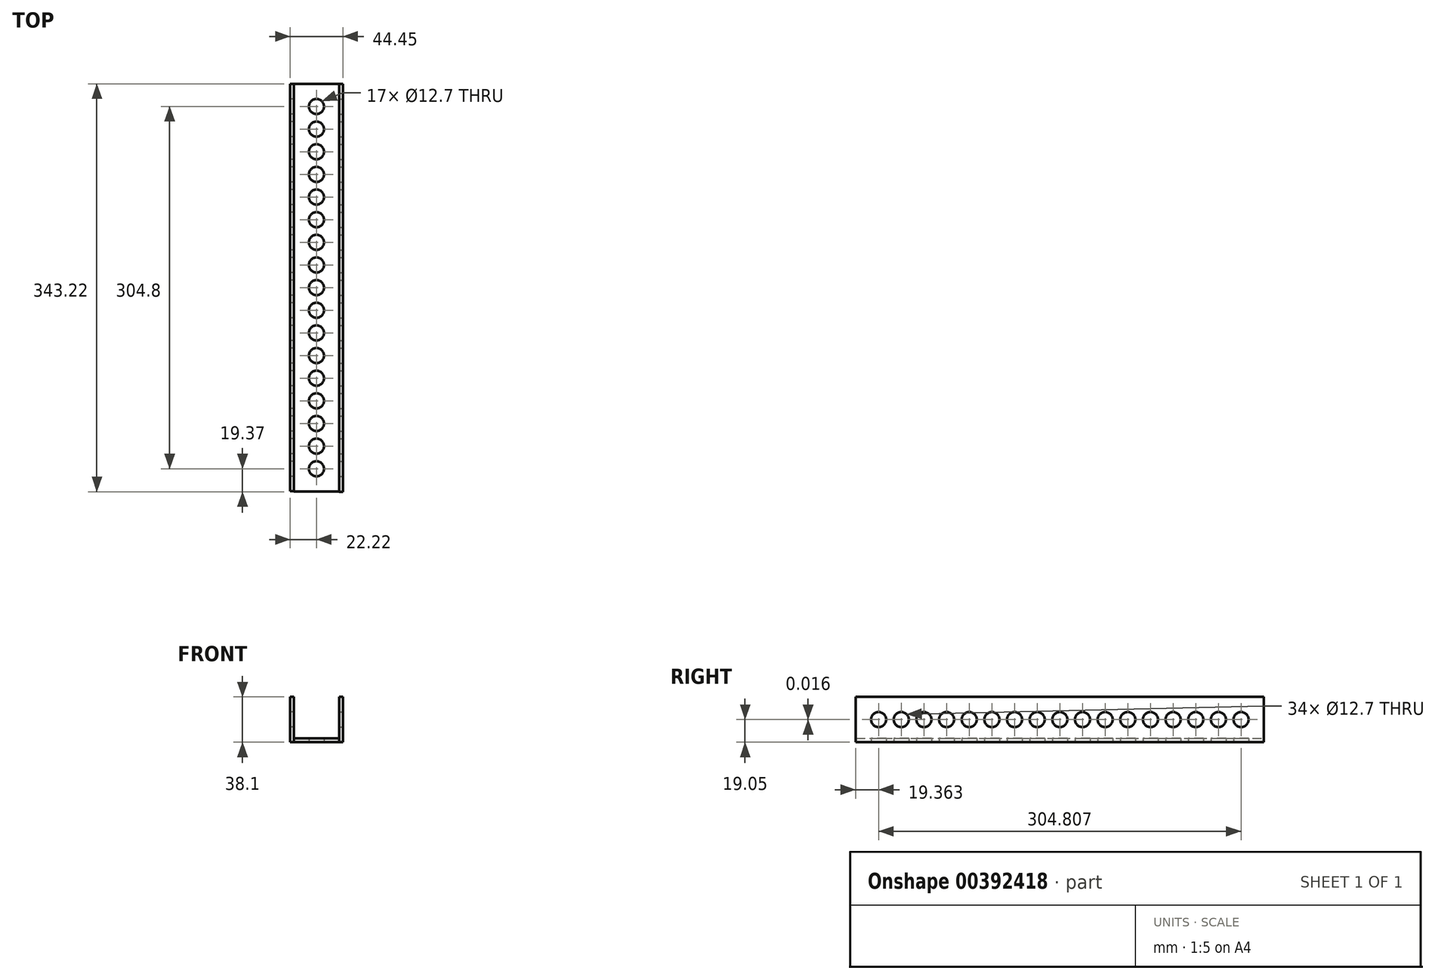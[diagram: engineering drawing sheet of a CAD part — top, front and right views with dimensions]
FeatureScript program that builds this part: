
annotation { "Feature Type Name" : "Feature", "Feature Type Description" : "" }
export const myFeature = defineFeature(function(context is Context, id is Id, definition is map)
    precondition{}
    {
        {
            var Q0;
            Q0=qCreatedBy(makeId("Top.planeOp"),FACE);
            var sketch = newSketch(context, id + "F0", { "sketchPlane" : qUnion([Q0])});
            skLineSegment(sketch, "E0.bottom", {"start": v(-89.28, 285.75) * mm, "end": v(-51.18, 285.75) * mm});
            skLineSegment(sketch, "E0.top", {"start": v(-89.28, -57.15) * mm, "end": v(-51.18, -57.15) * mm});
            skLineSegment(sketch, "E0.left", {"start": v(-89.28, 285.75) * mm, "end": v(-89.28, -57.15) * mm});
            skLineSegment(sketch, "E0.right", {"start": v(-51.18, 285.75) * mm, "end": v(-51.18, -57.15) * mm});
            skCircle(sketch, "E1", {"center": v(-70.23, 266.7) * mm, "radius": 6.35 * mm});
            skCircle(sketch, "E2", {"center": v(-70.23, 247.65) * mm, "radius": 6.35 * mm});
            skCircle(sketch, "E3", {"center": v(-70.23, 228.6) * mm, "radius": 6.35 * mm});
            skCircle(sketch, "E4", {"center": v(-70.23, 209.55) * mm, "radius": 6.35 * mm});
            skCircle(sketch, "E5", {"center": v(-70.23, 152.4) * mm, "radius": 6.35 * mm});
            skCircle(sketch, "E6", {"center": v(-70.23, 171.45) * mm, "radius": 6.35 * mm});
            skCircle(sketch, "E7", {"center": v(-70.23, 190.5) * mm, "radius": 6.35 * mm});
            skPoint(sketch, "E8", {"position": v(-89.28, 114.3) * mm});
            skCircle(sketch, "E9", {"center": v(-70.23, 95.25) * mm, "radius": 6.35 * mm});
            skCircle(sketch, "E10", {"center": v(-70.23, 76.2) * mm, "radius": 6.35 * mm});
            skCircle(sketch, "E11", {"center": v(-70.23, 114.3) * mm, "radius": 6.35 * mm});
            skCircle(sketch, "E12", {"center": v(-70.23, 57.15) * mm, "radius": 6.35 * mm});
            skCircle(sketch, "E13", {"center": v(-70.23, 0) * mm, "radius": 6.35 * mm});
            skCircle(sketch, "E14", {"center": v(-70.23, 38.1) * mm, "radius": 6.35 * mm});
            skCircle(sketch, "E15", {"center": v(-70.23, 19.05) * mm, "radius": 6.35 * mm});
            skCircle(sketch, "E16", {"center": v(-70.23, -38.1) * mm, "radius": 6.35 * mm});
            skCircle(sketch, "E17", {"center": v(-70.23, -19.05) * mm, "radius": 6.35 * mm});
            skPoint(sketch, "E18", {"position": v(-70.23, 285.75) * mm});
            skPoint(sketch, "E19", {"position": v(-70.23, -57.15) * mm});
            skLineSegment(sketch, "E20", {"start": v(-70.23, 285.75) * mm, "end": v(-70.23, -57.15) * mm});
            skLineSegment(sketch, "E21", {"start": v(-70.23, 266.7) * mm, "end": v(-70.23, 247.65) * mm});
            skLineSegment(sketch, "E22", {"start": v(-70.23, 247.65) * mm, "end": v(-70.23, 228.6) * mm});
            skLineSegment(sketch, "E23.bottom", {"start": v(-89.28, 285.75) * mm, "end": v(-92.45, 285.75) * mm});
            skLineSegment(sketch, "E23.top", {"start": v(-89.28, -57) * mm, "end": v(-92.45, -57) * mm});
            skLineSegment(sketch, "E23.left", {"start": v(-89.28, 285.75) * mm, "end": v(-89.28, -57) * mm});
            skLineSegment(sketch, "E23.right", {"start": v(-92.45, 285.75) * mm, "end": v(-92.45, -57) * mm});
            skCircle(sketch, "E24", {"center": v(-70.23, 133.35) * mm, "radius": 6.35 * mm});
            skLineSegment(sketch, "E25.bottom", {"start": v(-51.18, 285.75) * mm, "end": v(-48, 285.75) * mm});
            skLineSegment(sketch, "E25.top", {"start": v(-51.18, -57.47) * mm, "end": v(-48, -57.47) * mm});
            skLineSegment(sketch, "E25.left", {"start": v(-51.18, 285.75) * mm, "end": v(-51.18, -57.47) * mm});
            skLineSegment(sketch, "E25.right", {"start": v(-48, 285.75) * mm, "end": v(-48, -57.47) * mm});
            skSolve(sketch);
        }
        {
            var Q0;
            Q0 = qSketchRegion(id + "F0", true);
            extrude(context, id + "F1", {"entities" : qUnion([Q0]), "depth" : 3.17 * mm});
        }
        {
            var Q0;
            Q0=makeQuery(id+"F0.imprint","IMPRINT",FACE,{"disambiguationData":[TD([[makeQuery(id+"F0.imprint","IMPRINT",EDGE,{"derivedFrom":sQuery(id+"F0.wireOp",EDGE,"E23.bottom")}),1.0]])]});
            extrude(context, id + "F2", {"entities" : qUnion([Q0]), "operationType" : NewBodyOperationType.ADD, "depth" : 38.1 * mm});
        }
        {
            var Q0;
            {var subQ0=sQuery(id+"F0.wireOp",EDGE,"E23.right");Q0=makeQuery(id+"F2.boolean.opBoolean","MERGE",FACE,{"derivedFrom":[makeQuery(id+"F1.opExtrude","SWEPT_FACE",FACE,{"disambiguationData":[OSD([subQ0])]}),makeQuery(id+"F2.opExtrude","SWEPT_FACE",FACE,{"disambiguationData":[OSD([subQ0])]})]});}
            var sketch = newSketch(context, id + "F3", { "sketchPlane" : qUnion([Q0])});
            skCircle(sketch, "E26", {"center": v(-266.7, 19.05) * mm, "radius": 6.35 * mm});
            skPoint(sketch, "E27", {"position": v(-285.75, 19.05) * mm});
            skPoint(sketch, "E28", {"position": v(57, 19.05) * mm});
            skLineSegment(sketch, "E29", {"start": v(-285.75, 19.05) * mm, "end": v(57, 19.05) * mm});
            skCircle(sketch, "E30", {"center": v(-247.65, 19.05) * mm, "radius": 6.35 * mm});
            skCircle(sketch, "E31", {"center": v(-228.6, 19.05) * mm, "radius": 6.35 * mm});
            skCircle(sketch, "E32", {"center": v(-209.55, 19.05) * mm, "radius": 6.35 * mm});
            skCircle(sketch, "E33", {"center": v(-190.5, 19.05) * mm, "radius": 6.35 * mm});
            skCircle(sketch, "E34", {"center": v(-171.45, 19.05) * mm, "radius": 6.35 * mm});
            skCircle(sketch, "E35", {"center": v(-152.4, 19.05) * mm, "radius": 6.35 * mm});
            skCircle(sketch, "E36", {"center": v(0, 19.05) * mm, "radius": 6.35 * mm});
            skCircle(sketch, "E37", {"center": v(-19.05, 19.05) * mm, "radius": 6.35 * mm});
            skCircle(sketch, "E38", {"center": v(19.05, 19.07) * mm, "radius": 6.35 * mm});
            skCircle(sketch, "E39", {"center": v(-38.1, 19.05) * mm, "radius": 6.35 * mm});
            skCircle(sketch, "E40", {"center": v(-133.35, 19.05) * mm, "radius": 6.35 * mm});
            skCircle(sketch, "E41", {"center": v(-95.25, 19.05) * mm, "radius": 6.35 * mm});
            skCircle(sketch, "E42", {"center": v(38.1, 19.05) * mm, "radius": 6.35 * mm});
            skCircle(sketch, "E43", {"center": v(-76.2, 19.05) * mm, "radius": 6.35 * mm});
            skCircle(sketch, "E44", {"center": v(-114.3, 19.05) * mm, "radius": 6.35 * mm});
            skCircle(sketch, "E45", {"center": v(-57.15, 19.05) * mm, "radius": 6.35 * mm});
            skSolve(sketch);
        }
        {
            var Q0;
            Q0 = qSketchRegion(id + "F3", true);
            extrude(context, id + "F4", {"entities" : qUnion([Q0]), "operationType" : NewBodyOperationType.REMOVE, "oppositeDirection" : true, "depth" : 12.7 * mm});
        }
        {
            var Q0;
            {var subQ3=sQuery(id+"F0.wireOp",EDGE,"E25.bottom");Q0=makeQuery(id+"F0.imprint","IMPRINT",FACE,{"disambiguationData":[TD([[makeQuery(id+"F0.imprint","IMPRINT",EDGE,{"derivedFrom":subQ3}),-1.0]])]});}
            extrude(context, id + "F5", {"entities" : qUnion([Q0]), "operationType" : NewBodyOperationType.ADD, "depth" : 38.1 * mm});
        }
        {
            var Q0;
            {var subQ0=sQuery(id+"F0.wireOp",EDGE,"E25.right");Q0=makeQuery(id+"F5.boolean.opBoolean","MERGE",FACE,{"derivedFrom":[makeQuery(id+"F1.opExtrude","SWEPT_FACE",FACE,{"disambiguationData":[OSD([subQ0])]}),makeQuery(id+"F5.opExtrude","SWEPT_FACE",FACE,{"disambiguationData":[OSD([subQ0])]})]});}
            var sketch = newSketch(context, id + "F6", { "sketchPlane" : qUnion([Q0])});
            skCircle(sketch, "E46", {"center": v(266.7, 19.05) * mm, "radius": 6.35 * mm});
            skPoint(sketch, "E47", {"position": v(285.75, 19.05) * mm});
            skPoint(sketch, "E48", {"position": v(-57.47, 19.05) * mm});
            skLineSegment(sketch, "E49", {"start": v(285.75, 19.05) * mm, "end": v(-57.47, 19.05) * mm});
            skCircle(sketch, "E50", {"center": v(247.65, 19.05) * mm, "radius": 6.35 * mm});
            skCircle(sketch, "E51", {"center": v(209.54, 19.05) * mm, "radius": 6.35 * mm});
            skCircle(sketch, "E52", {"center": v(190.5, 19.05) * mm, "radius": 6.35 * mm});
            skCircle(sketch, "E53", {"center": v(152.4, 19.05) * mm, "radius": 6.35 * mm});
            skCircle(sketch, "E54", {"center": v(133.34, 19.05) * mm, "radius": 6.35 * mm});
            skCircle(sketch, "E55", {"center": v(114.3, 19.05) * mm, "radius": 6.35 * mm});
            skCircle(sketch, "E56", {"center": v(95.24, 19.05) * mm, "radius": 6.35 * mm});
            skCircle(sketch, "E57", {"center": v(76.2, 19.05) * mm, "radius": 6.35 * mm});
            skCircle(sketch, "E58", {"center": v(57.14, 19.05) * mm, "radius": 6.35 * mm});
            skCircle(sketch, "E59", {"center": v(19.04, 19.05) * mm, "radius": 6.35 * mm});
            skCircle(sketch, "E60", {"center": v(0, 19.05) * mm, "radius": 6.35 * mm});
            skCircle(sketch, "E61", {"center": v(38.1, 19.05) * mm, "radius": 6.35 * mm});
            skCircle(sketch, "E62", {"center": v(228.6, 19.05) * mm, "radius": 6.35 * mm});
            skCircle(sketch, "E63", {"center": v(171.44, 19.05) * mm, "radius": 6.35 * mm});
            skCircle(sketch, "E64", {"center": v(-19.06, 19.05) * mm, "radius": 6.35 * mm});
            skCircle(sketch, "E65", {"center": v(-38.1, 19.05) * mm, "radius": 6.35 * mm});
            skSolve(sketch);
        }
        {
            var Q0;
            Q0 = qSketchRegion(id + "F6", true);
            extrude(context, id + "F7", {"entities" : qUnion([Q0]), "operationType" : NewBodyOperationType.REMOVE, "oppositeDirection" : true, "depth" : 12.7 * mm});
        }
    });
